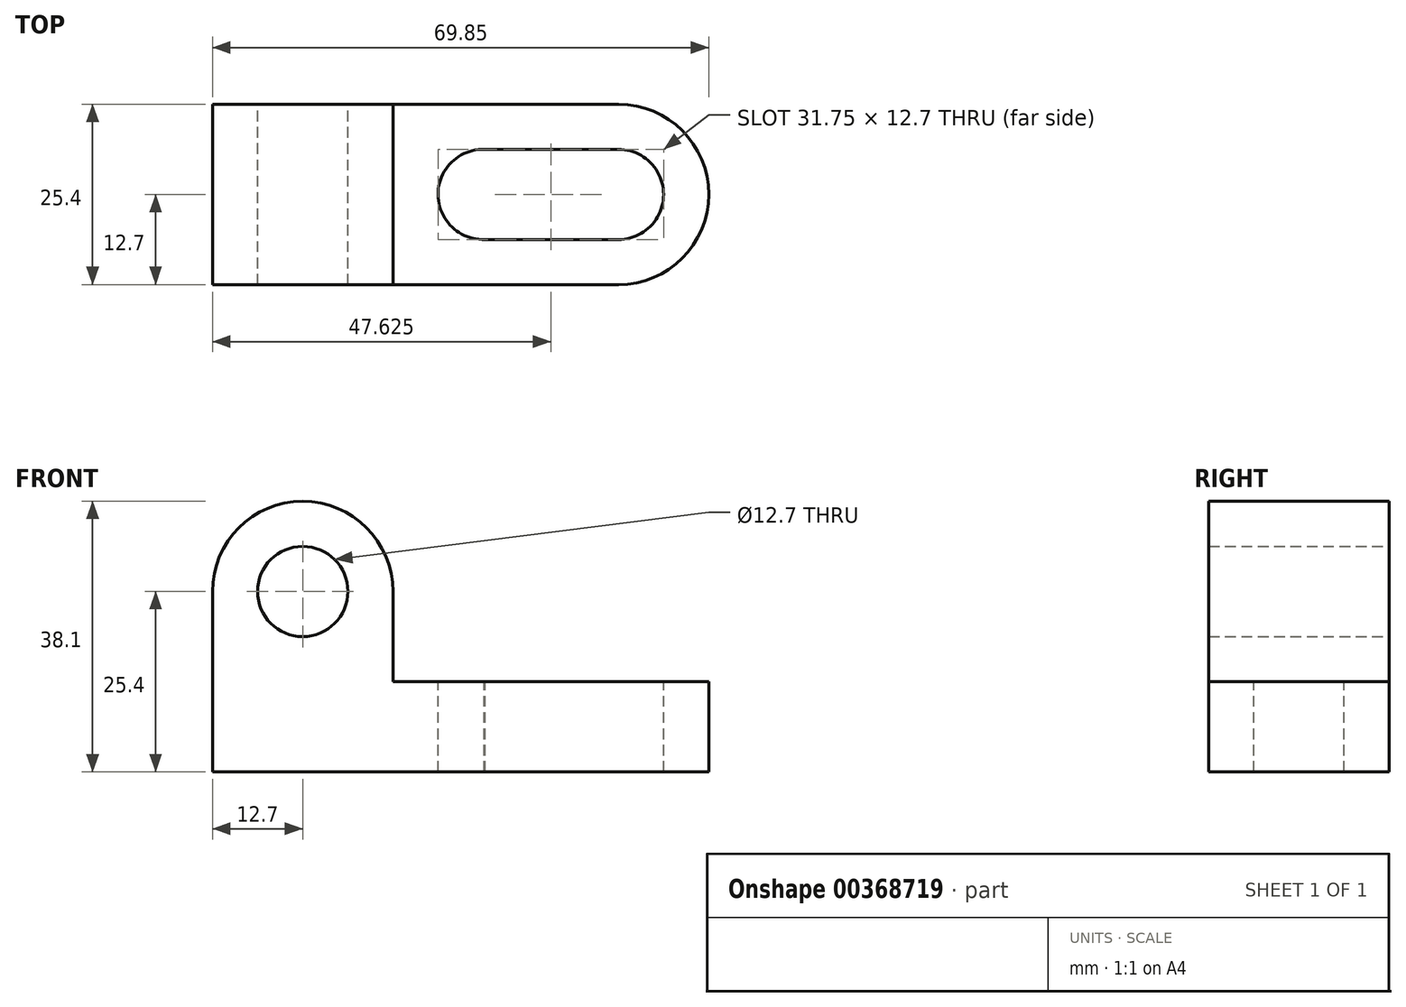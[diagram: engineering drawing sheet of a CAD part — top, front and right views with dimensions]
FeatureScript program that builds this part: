
annotation { "Feature Type Name" : "Feature", "Feature Type Description" : "" }
export const myFeature = defineFeature(function(context is Context, id is Id, definition is map)
    precondition{}
    {
        {
            var Q0;
            Q0=qCreatedBy(makeId("Front.planeOp"),FACE);
            var sketch = newSketch(context, id + "F0", { "sketchPlane" : qUnion([Q0])});
            skLineSegment(sketch, "E0", {"start": v(0, 0) * mm, "end": v(25.4, 0) * mm});
            skLineSegment(sketch, "E1", {"start": v(25.4, 0) * mm, "end": v(25.4, 25.4) * mm});
            skLineSegment(sketch, "E2", {"start": v(19.05, 25.4) * mm, "end": v(12.7, 25.4) * mm});
            skLineSegment(sketch, "E3", {"start": v(0, 25.4) * mm, "end": v(0, 0) * mm});
            skCircle(sketch, "E4", {"center": v(12.7, 25.4) * mm, "radius": 6.35 * mm});
            skArc(sketch, "E5", {"start": v(25.4, 25.4) * mm, "mid": v(12.7, 38.1) * mm, "end": v(0, 25.4) * mm});
            skSolve(sketch);
        }
        {
            var Q0;
            Q0=makeQuery(id+"F0.imprint","IMPRINT",FACE,{"disambiguationData":[TD([[makeQuery(id+"F0.imprint","IMPRINT",EDGE,{"derivedFrom":sQuery(id+"F0.wireOp",EDGE,"E0")}),1.0]])]});
            extrude(context, id + "F1", {"entities" : qUnion([Q0]), "depth" : 25.4 * mm});
        }
        {
            var Q0;
            Q0=makeQuery(id+"F1.opExtrude","SWEPT_FACE",FACE,{"disambiguationData":[OSD([sQuery(id+"F0.wireOp",EDGE,"E1")])]});
            var sketch = newSketch(context, id + "F2", { "sketchPlane" : qUnion([Q0])});
            skLineSegment(sketch, "E6", {"start": v(-25.4, 0) * mm, "end": v(-25.4, 12.7) * mm});
            skLineSegment(sketch, "E7", {"start": v(-25.4, 12.7) * mm, "end": v(0, 12.7) * mm});
            skLineSegment(sketch, "E8", {"start": v(0, 12.7) * mm, "end": v(0, 0) * mm});
            skLineSegment(sketch, "E9", {"start": v(0, 0) * mm, "end": v(-25.4, 0) * mm});
            skSolve(sketch);
        }
        {
            var Q0;
            Q0 = qSketchRegion(id + "F2", true);
            extrude(context, id + "F3", {"entities" : qUnion([Q0]), "operationType" : NewBodyOperationType.ADD, "depth" : 44.45 * mm});
        }
        {
            var Q0;
            Q0=makeQuery(id+"F3.opExtrude","CAP_EDGE",EDGE,{"disambiguationData":[OSD([sQuery(id+"F2.wireOp",EDGE,"E6")])],"isStart":false});
            var Q1;
            Q1=makeQuery(id+"F3.opExtrude","CAP_EDGE",EDGE,{"disambiguationData":[OSD([sQuery(id+"F2.wireOp",EDGE,"E8")])],"isStart":false});
            fillet(context, id + "F4", {"entities" : qUnion([Q0, Q1]), "radius" : 12.7 * mm, "tangentPropagation" : true, "allowEdgeOverflow" : false});
        }
        {
            var Q0;
            Q0=makeQuery(id+"F3.opExtrude","SWEPT_FACE",FACE,{"disambiguationData":[OSD([sQuery(id+"F2.wireOp",EDGE,"E7")])]});
            var sketch = newSketch(context, id + "F5", { "sketchPlane" : qUnion([Q0])});
            skCircle(sketch, "E10", {"center": v(38.1, -12.7) * mm, "radius": 6.35 * mm});
            skCircle(sketch, "E11", {"center": v(57.15, -12.7) * mm, "radius": 6.35 * mm});
            skLineSegment(sketch, "E12", {"start": v(37.94, -6.35) * mm, "end": v(57.15, -6.35) * mm});
            skLineSegment(sketch, "E13", {"start": v(37.84, -19.04) * mm, "end": v(57.15, -19.05) * mm});
            skPoint(sketch, "E14.orphan", {"position": v(69.85, -12.7) * mm});
            skPoint(sketch, "E15.start.orphan", {"position": v(25.4, -12.7) * mm});
            skSolve(sketch);
        }
        {
            var Q0;
            Q0 = qSketchRegion(id + "F5", true);
            extrude(context, id + "F6", {"entities" : qUnion([Q0]), "operationType" : NewBodyOperationType.REMOVE, "oppositeDirection" : true, "depth" : 25.4 * mm});
        }
    });
